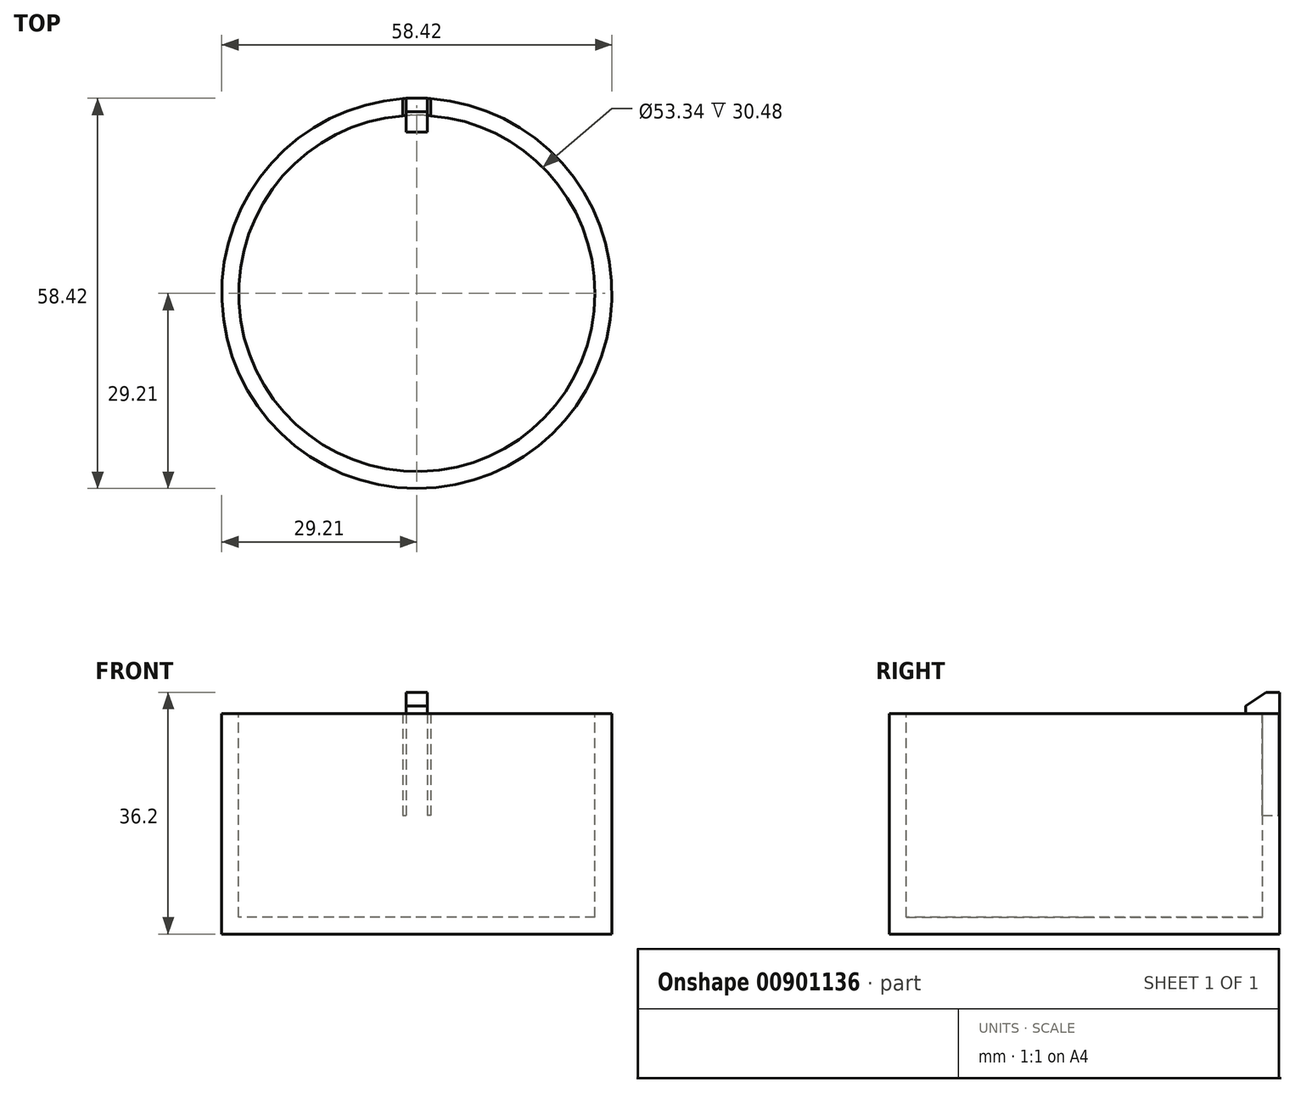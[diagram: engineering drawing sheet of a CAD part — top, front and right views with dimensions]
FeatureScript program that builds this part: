
annotation { "Feature Type Name" : "Feature", "Feature Type Description" : "" }
export const myFeature = defineFeature(function(context is Context, id is Id, definition is map)
    precondition{}
    {
        {
            var Q0;
            Q0=qCreatedBy(makeId("Top.planeOp"),FACE);
            var sketch = newSketch(context, id + "F0", { "sketchPlane" : qUnion([Q0])});
            skCircle(sketch, "E0", {"center": v(0, 0) * mm, "radius": 29.21 * mm});
            skSolve(sketch);
        }
        {
            var Q0;
            Q0 = qSketchRegion(id + "F0", true);
            extrude(context, id + "F1", {"entities" : qUnion([Q0]), "depth" : 33.02 * mm, "offsetDistance" : 25.4 * mm});
        }
        {
            var Q0;
            Q0=makeQuery(id+"F1.opExtrude","CAP_FACE",FACE,{"disambiguationData":[OSD([sQuery(id+"F0.wireOp",EDGE,"E0")])],"isStart":false});
            var sketch = newSketch(context, id + "F2", { "sketchPlane" : qUnion([Q0])});
            skCircle(sketch, "E1", {"center": v(0, 0) * mm, "radius": 26.67 * mm});
            skSolve(sketch);
        }
        {
            var Q0;
            Q0 = qSketchRegion(id + "F2", true);
            extrude(context, id + "F3", {"entities" : qUnion([Q0]), "operationType" : NewBodyOperationType.REMOVE, "oppositeDirection" : true, "depth" : 30.48 * mm, "offsetDistance" : 25.4 * mm});
        }
        {
            var Q0;
            Q0=makeQuery(id+"F1.opExtrude","CAP_FACE",FACE,{"disambiguationData":[OSD([sQuery(id+"F0.wireOp",EDGE,"E0")])],"isStart":false});
            var sketch = newSketch(context, id + "F4", { "sketchPlane" : qUnion([Q0])});
            skLineSegment(sketch, "E2.bottom", {"start": v(-1.59, 29.21) * mm, "end": v(1.59, 29.21) * mm});
            skLineSegment(sketch, "E2.top", {"start": v(-1.59, 24.13) * mm, "end": v(1.59, 24.13) * mm});
            skLineSegment(sketch, "E2.left", {"start": v(-1.59, 29.21) * mm, "end": v(-1.59, 24.13) * mm});
            skLineSegment(sketch, "E2.right", {"start": v(1.59, 29.21) * mm, "end": v(1.59, 24.13) * mm});
            skPoint(sketch, "E3", {"position": v(0, 29.21) * mm});
            skSolve(sketch);
        }
        {
            var Q0;
            Q0 = qSketchRegion(id + "F4", true);
            extrude(context, id + "F5", {"entities" : qUnion([Q0]), "operationType" : NewBodyOperationType.ADD, "depth" : 3.17 * mm, "offsetDistance" : 25.4 * mm});
        }
        {
            var Q0;
            Q0=makeQuery(id+"F5.opExtrude","SWEPT_FACE",FACE,{"disambiguationData":[OSD([sQuery(id+"F4.wireOp",EDGE,"E2.left")])]});
            var sketch = newSketch(context, id + "F6", { "sketchPlane" : qUnion([Q0])});
            skLineSegment(sketch, "E4", {"start": v(-27.18, 36.2) * mm, "end": v(-24.13, 34.16) * mm});
            skLineSegment(sketch, "E5", {"start": v(-24.13, 34.16) * mm, "end": v(-24.13, 36.2) * mm});
            skLineSegment(sketch, "E6", {"start": v(-24.13, 36.2) * mm, "end": v(-27.18, 36.2) * mm});
            skSolve(sketch);
        }
        {
            var Q0;
            Q0=makeQuery(id+"F6.imprint","IMPRINT",FACE,{"disambiguationData":[TD([[makeQuery(id+"F6.imprint","IMPRINT",EDGE,{"derivedFrom":sQuery(id+"F6.wireOp",EDGE,"E4")}),1.0]])]});
            extrude(context, id + "F7", {"entities" : qUnion([Q0]), "operationType" : NewBodyOperationType.REMOVE, "endBound" : BoundingType.UP_TO_NEXT, "oppositeDirection" : true, "depth" : 25.4 * mm, "offsetDistance" : 25.4 * mm});
        }
        {
            var Q0;
            Q0=makeQuery(id+"F5.opExtrude","SWEPT_FACE",FACE,{"disambiguationData":[OSD([sQuery(id+"F4.wireOp",EDGE,"E2.bottom")])]});
            var sketch = newSketch(context, id + "F8", { "sketchPlane" : qUnion([Q0])});
            skLineSegment(sketch, "E7.bottom", {"start": v(1.59, 33.02) * mm, "end": v(2.1, 33.02) * mm});
            skLineSegment(sketch, "E7.top", {"start": v(1.59, 17.78) * mm, "end": v(2.1, 17.78) * mm});
            skLineSegment(sketch, "E7.left", {"start": v(1.59, 33.02) * mm, "end": v(1.59, 17.78) * mm});
            skLineSegment(sketch, "E7.right", {"start": v(2.1, 33.02) * mm, "end": v(2.1, 17.78) * mm});
            skLineSegment(sketch, "E8.bottom", {"start": v(-1.59, 33.02) * mm, "end": v(-2.1, 33.02) * mm});
            skLineSegment(sketch, "E8.top", {"start": v(-1.59, 17.78) * mm, "end": v(-2.1, 17.78) * mm});
            skLineSegment(sketch, "E8.left", {"start": v(-1.59, 33.02) * mm, "end": v(-1.59, 17.78) * mm});
            skLineSegment(sketch, "E8.right", {"start": v(-2.1, 33.02) * mm, "end": v(-2.1, 17.78) * mm});
            skSolve(sketch);
        }
        {
            var Q0;
            Q0 = qSketchRegion(id + "F8", true);
            extrude(context, id + "F9", {"entities" : qUnion([Q0]), "operationType" : NewBodyOperationType.REMOVE, "oppositeDirection" : true, "depth" : 5.08 * mm, "offsetDistance" : 25.4 * mm});
        }
    });
